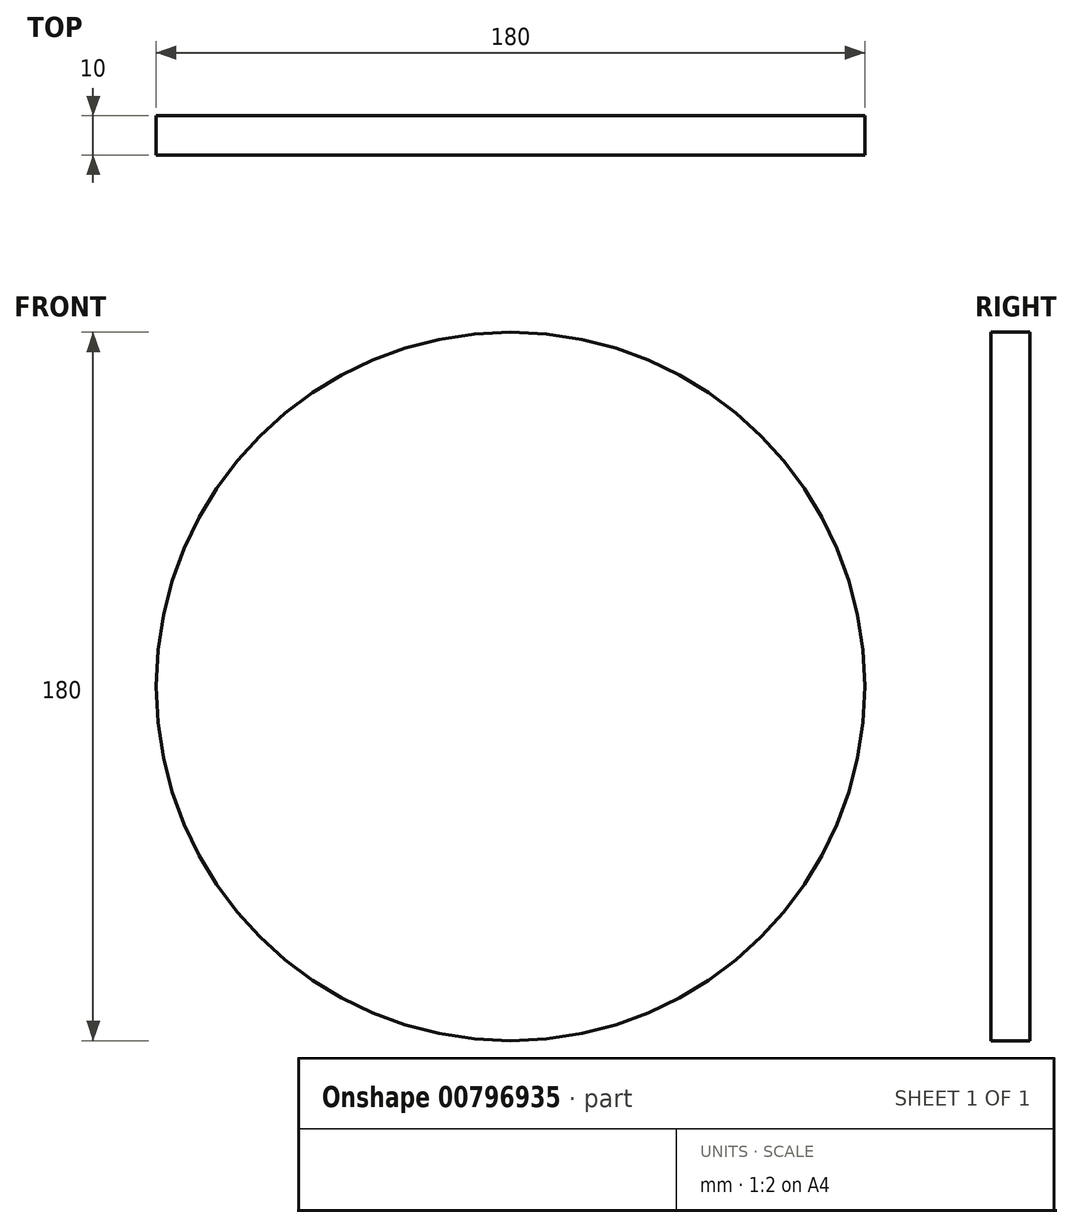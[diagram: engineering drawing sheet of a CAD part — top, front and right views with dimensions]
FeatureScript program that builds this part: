
annotation { "Feature Type Name" : "Feature", "Feature Type Description" : "" }
export const myFeature = defineFeature(function(context is Context, id is Id, definition is map)
    precondition{}
    {
        {
            var Q0;
            Q0=qCreatedBy(makeId("Front.planeOp"),FACE);
            var sketch = newSketch(context, id + "F0", { "sketchPlane" : qUnion([Q0])});
            skCircle(sketch, "E0", {"center": v(0, 0) * mm, "radius": 90 * mm});
            skSolve(sketch);
        }
        {
            var Q0;
            Q0 = qSketchRegion(id + "F0", true);
            extrude(context, id + "F1", {"entities" : qUnion([Q0]), "depth" : 10 * mm, "offsetDistance" : 25 * mm});
        }
    });
